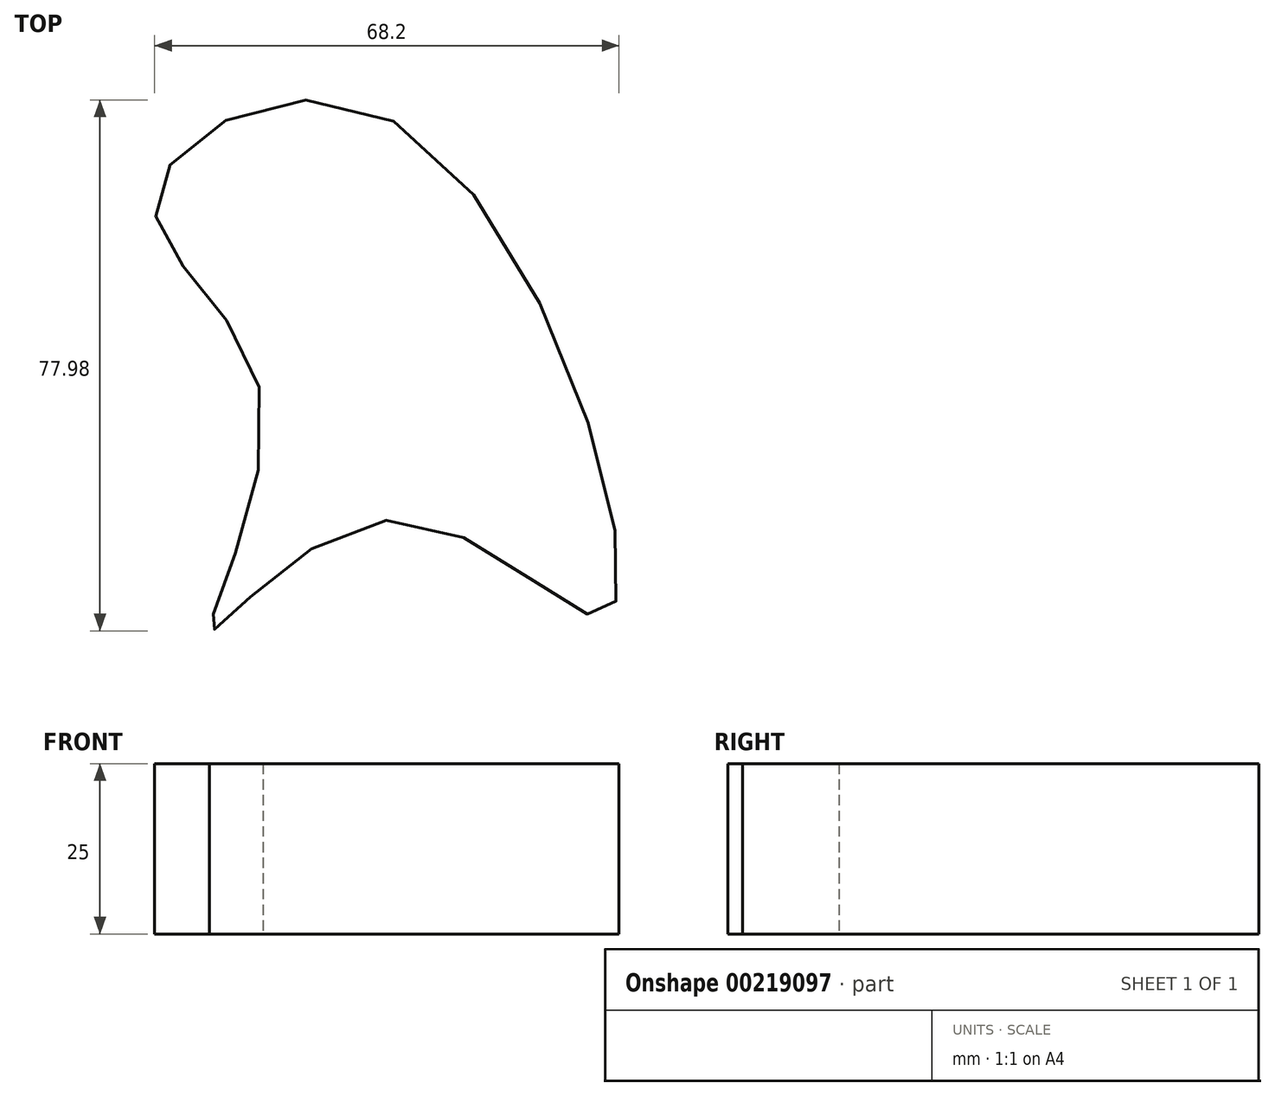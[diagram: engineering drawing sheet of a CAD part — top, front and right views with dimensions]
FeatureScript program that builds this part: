
annotation { "Feature Type Name" : "Feature", "Feature Type Description" : "" }
export const myFeature = defineFeature(function(context is Context, id is Id, definition is map)
    precondition{}
    {
        {
            var Q0;
            Q0=qCreatedBy(makeId("Top.planeOp"),FACE);
            var sketch = newSketch(context, id + "F0", { "sketchPlane" : qUnion([Q0])});
            skFitSpline(sketch, "E0", {"points": [v(0, 40.57) * mm, v(-35.01, 29.09) * mm, v(-19.45, 0) * mm, v(-26.86, -34.27) * mm, v(0, -17.97) * mm, v(31.68, -31.68) * mm, v(0, 40.57) * mm]});
            skSolve(sketch);
        }
        {
            var Q0;
            Q0=makeQuery(id+"F0.imprint","IMPRINT",FACE,{"disambiguationData":[TD([[makeQuery(id+"F0.imprint","IMPRINT",EDGE,{"derivedFrom":sQuery(id+"F0.wireOp",EDGE,"E0")}),1.0]])]});
            extrude(context, id + "F1", {"entities" : qUnion([Q0]), "depth" : 25 * mm});
        }
    });
